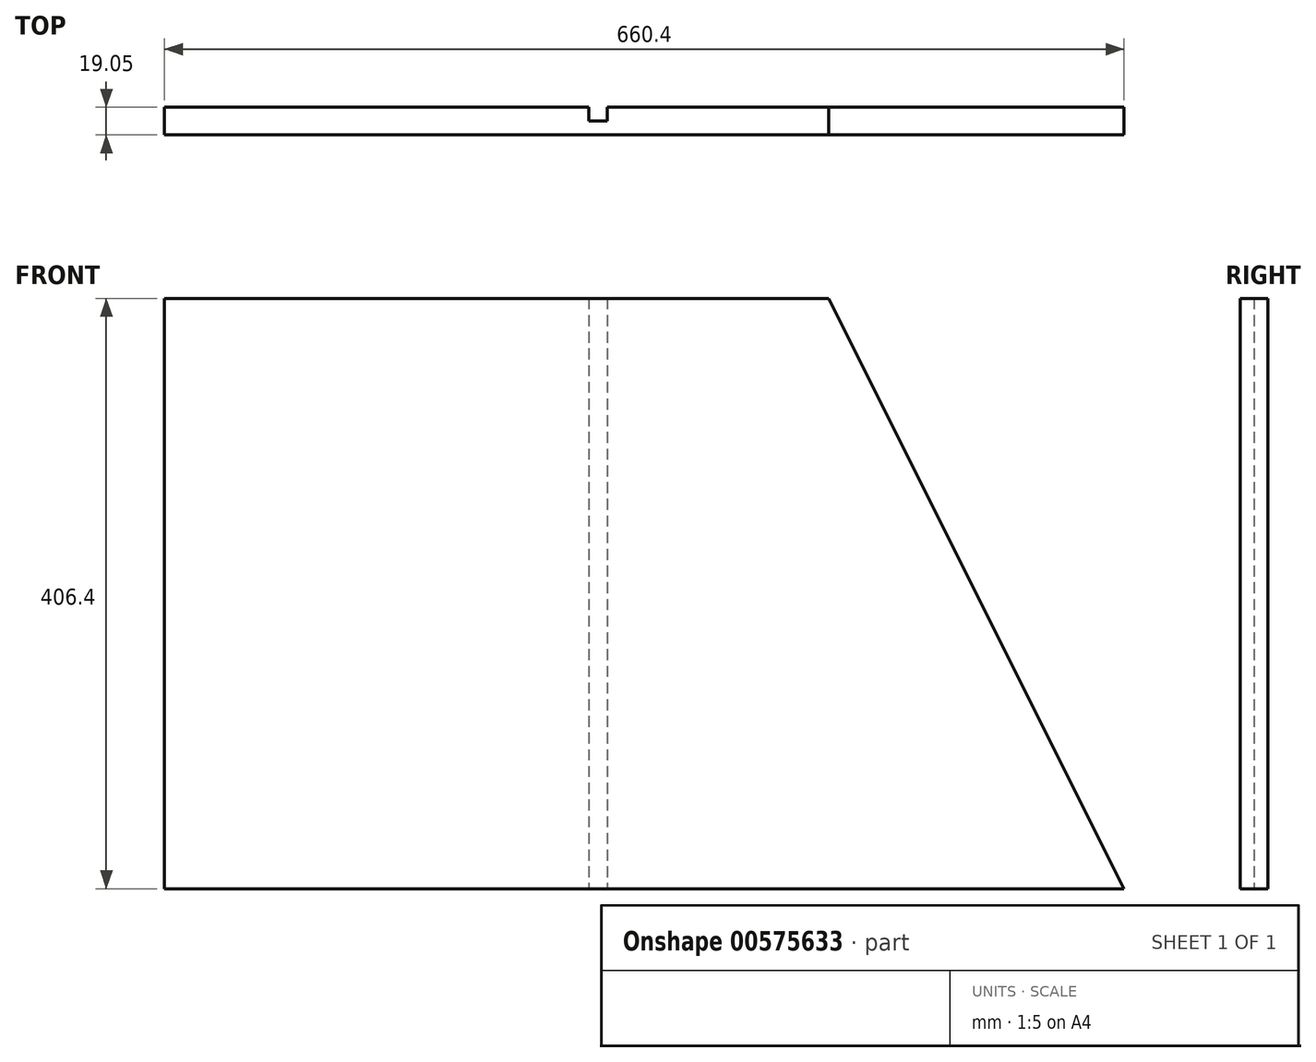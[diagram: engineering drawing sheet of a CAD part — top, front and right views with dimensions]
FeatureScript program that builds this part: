
annotation { "Feature Type Name" : "Feature", "Feature Type Description" : "" }
export const myFeature = defineFeature(function(context is Context, id is Id, definition is map)
    precondition{}
    {
        {
            var Q0;
            Q0=qCreatedBy(makeId("Front.planeOp"),FACE);
            var sketch = newSketch(context, id + "F0", { "sketchPlane" : qUnion([Q0])});
            skLineSegment(sketch, "E0", {"start": v(-356.65, 252.41) * mm, "end": v(-229.65, 252.41) * mm});
            skLineSegment(sketch, "E1", {"start": v(-229.65, 252.41) * mm, "end": v(-26.45, -153.99) * mm});
            skLineSegment(sketch, "E2", {"start": v(-26.45, -153.99) * mm, "end": v(-686.85, -153.99) * mm});
            skLineSegment(sketch, "E3", {"start": v(-229.65, 252.41) * mm, "end": v(-229.65, -153.99) * mm, "construction": true});
            skLineSegment(sketch, "E4.bottom", {"start": v(-356.65, 252.41) * mm, "end": v(-686.85, 252.41) * mm});
            skLineSegment(sketch, "E4.top", {"start": v(-356.65, -153.99) * mm, "end": v(-686.85, -153.99) * mm});
            skLineSegment(sketch, "E4.right", {"start": v(-686.85, 252.41) * mm, "end": v(-686.85, -153.99) * mm});
            skSolve(sketch);
        }
        {
            var Q0;
            {var subQ0=sQuery(id+"F0.wireOp",EDGE,"nFMApCBA-aBbS-xDlN-ZNX0-Un9WT2dHDHLE");Q0=makeQuery(id+"F0.imprint","IMPRINT",FACE,{"disambiguationData":[TD([[makeQuery(id+"F0.imprint","IMPRINT",EDGE,{"derivedFrom":subQ0}),-1.0]])]});}
            var Q1;
            Q1=makeQuery(id+"F0.imprint","IMPRINT",FACE,{"disambiguationData":[TD([[makeQuery(id+"F0.imprint","IMPRINT",EDGE,{"derivedFrom":sQuery(id+"F0.wireOp",EDGE,"E0")}),-1.0]])]});
            var Q2;
            {var subQ0=sQuery(id+"F0.wireOp",EDGE,"E1");Q2=makeQuery(id+"F0.imprint","IMPRINT",FACE,{"disambiguationData":[TD([[makeQuery(id+"F0.imprint","IMPRINT",EDGE,{"derivedFrom":subQ0}),-1.0]])]});}
            extrude(context, id + "F1", {"entities" : qUnion([Q0, Q1, Q2]), "depth" : 19.05 * mm, "offsetDistance" : 25.4 * mm});
        }
        {
            var Q0;
            Q0=makeQuery(id+"F1.opExtrude","CAP_FACE",FACE,{"disambiguationData":[OSD([sQuery(id+"F0.wireOp",EDGE,"E0"),sQuery(id+"F0.wireOp",EDGE,"E1"),sQuery(id+"F0.wireOp",EDGE,"E2"),sQuery(id+"F0.wireOp",EDGE,"nFMApCBA-aBbS-xDlN-ZNX0-Un9WT2dHDHLE")])],"isStart":true});
            var sketch = newSketch(context, id + "F2", { "sketchPlane" : qUnion([Q0])});
            skLineSegment(sketch, "E5", {"start": v(229.65, 252.41) * mm, "end": v(229.65, -153.99) * mm});
            skLineSegment(sketch, "E6.0", {"start": v(382.05, 252.41) * mm, "end": v(382.05, -153.99) * mm});
            skLineSegment(sketch, "E7.0", {"start": v(394.75, 252.41) * mm, "end": v(394.75, -153.99) * mm});
            skLineSegment(sketch, "E8.bottom", {"start": v(394.75, 252.41) * mm, "end": v(382.05, 252.41) * mm});
            skLineSegment(sketch, "E8.top", {"start": v(394.75, -153.99) * mm, "end": v(382.05, -153.99) * mm});
            skSolve(sketch);
        }
        {
            var Q0;
            Q0=qSketchRegion(id+"F2",true);
            extrude(context, id + "F3", {"entities" : qUnion([Q0]), "operationType" : NewBodyOperationType.REMOVE, "oppositeDirection" : true, "depth" : 9.52 * mm, "offsetDistance" : 25.4 * mm});
        }
    });
